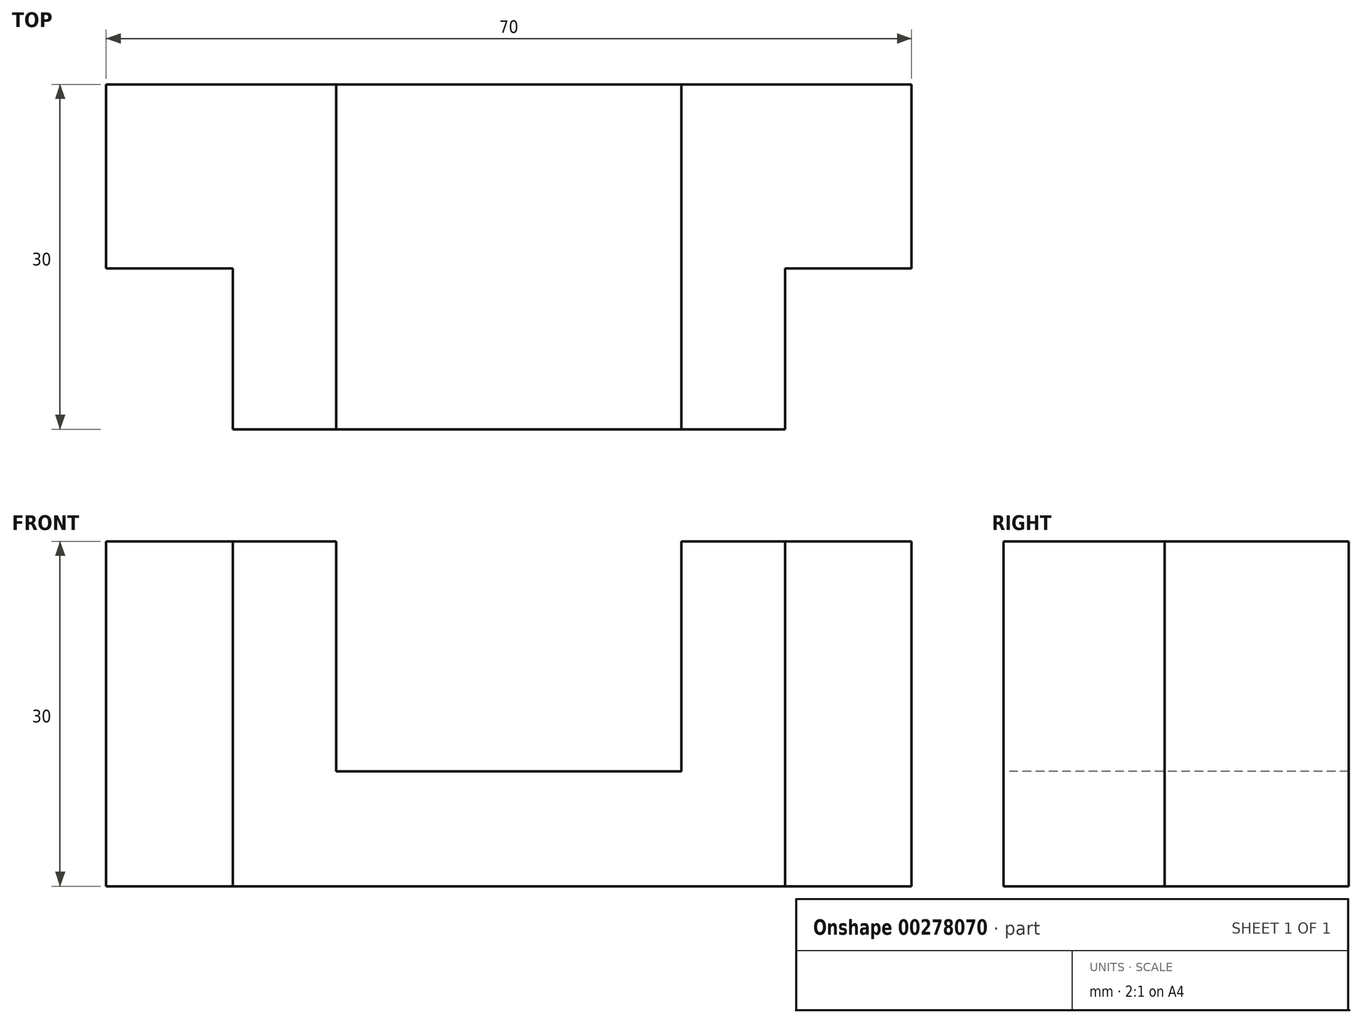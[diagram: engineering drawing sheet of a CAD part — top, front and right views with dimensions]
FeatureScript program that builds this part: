
annotation { "Feature Type Name" : "Feature", "Feature Type Description" : "" }
export const myFeature = defineFeature(function(context is Context, id is Id, definition is map)
    precondition{}
    {
        {
            var Q0;
            Q0=qCreatedBy(makeId("Front.planeOp"),FACE);
            var sketch = newSketch(context, id + "F0", { "sketchPlane" : qUnion([Q0])});
            skLineSegment(sketch, "E0", {"start": v(-35, 15) * mm, "end": v(-35, -15) * mm});
            skLineSegment(sketch, "E1", {"start": v(-35, -15) * mm, "end": v(35, -15) * mm});
            skLineSegment(sketch, "E2", {"start": v(35, -15) * mm, "end": v(35, 15) * mm});
            skLineSegment(sketch, "E3", {"start": v(35, 15) * mm, "end": v(-35, 15) * mm});
            skSolve(sketch);
        }
        {
            var Q0;
            Q0 = qSketchRegion(id + "F0", true);
            extrude(context, id + "F1", {"entities" : qUnion([Q0]), "depth" : 30 * mm});
        }
        {
            var Q0;
            Q0=makeQuery(id+"F1.opExtrude","SWEPT_FACE",FACE,{"disambiguationData":[OSD([sQuery(id+"F0.wireOp",EDGE,"E3")])]});
            var sketch = newSketch(context, id + "F2", { "sketchPlane" : qUnion([Q0])});
            skLineSegment(sketch, "E4", {"start": v(-15, 0) * mm, "end": v(-15, -30) * mm});
            skLineSegment(sketch, "E5", {"start": v(-15, -30) * mm, "end": v(15, -30) * mm});
            skLineSegment(sketch, "E6", {"start": v(15, -30) * mm, "end": v(15, 0) * mm});
            skLineSegment(sketch, "E7", {"start": v(-15, 0) * mm, "end": v(15, 0) * mm});
            skSolve(sketch);
        }
        {
            var Q0;
            Q0=makeQuery(id+"F2.imprint","IMPRINT",FACE,{"disambiguationData":[TD([[makeQuery(id+"F2.imprint","IMPRINT",EDGE,{"derivedFrom":sQuery(id+"F2.wireOp",EDGE,"E4")}),1.0]])]});
            extrude(context, id + "F3", {"entities" : qUnion([Q0]), "operationType" : NewBodyOperationType.REMOVE, "oppositeDirection" : true, "depth" : 20 * mm});
        }
        {
            var Q0;
            Q0=makeQuery(id+"F2.imprint","IMPRINT",FACE,{"disambiguationData":[TD([[makeQuery(id+"F2.imprint","IMPRINT",EDGE,{"derivedFrom":sQuery(id+"F2.wireOp",EDGE,"E4")}),1.0]])]});
            extrude(context, id + "F4", {"entities" : qUnion([Q0]), "operationType" : NewBodyOperationType.REMOVE, "oppositeDirection" : true, "depth" : 20 * mm});
        }
        {
            var Q0;
            {var subQ0=sQuery(id+"F0.wireOp",EDGE,"E3");var subQ1=sQuery(id+"F0.wireOp",EDGE,"E2");Q0=makeQuery(id+"F4.boolean.opBoolean","SPLIT",FACE,{"disambiguationData":[TD([makeQuery(id+"F1.opExtrude","SWEPT_FACE",FACE,{"disambiguationData":[OSD([subQ1])]})])],"derivedFrom":makeQuery(id+"F1.opExtrude","SWEPT_FACE",FACE,{"disambiguationData":[OSD([subQ0])]})});}
            var sketch = newSketch(context, id + "F5", { "sketchPlane" : qUnion([Q0])});
            skLineSegment(sketch, "E8", {"start": v(24, -30) * mm, "end": v(24, -16) * mm});
            skLineSegment(sketch, "E9", {"start": v(24, -16) * mm, "end": v(35, -16) * mm});
            skLineSegment(sketch, "E10", {"start": v(24, -30) * mm, "end": v(35, -30) * mm});
            skLineSegment(sketch, "E11", {"start": v(35, -30) * mm, "end": v(35, -16) * mm});
            skSolve(sketch);
        }
        {
            var Q0;
            Q0=makeQuery(id+"F5.imprint","IMPRINT",FACE,{"disambiguationData":[TD([[makeQuery(id+"F5.imprint","IMPRINT",EDGE,{"derivedFrom":sQuery(id+"F5.wireOp",EDGE,"E8")}),-1.0]])]});
            extrude(context, id + "F6", {"entities" : qUnion([Q0]), "operationType" : NewBodyOperationType.REMOVE, "oppositeDirection" : true, "depth" : 30 * mm});
        }
        {
            var Q0;
            {var subQ0=sQuery(id+"F0.wireOp",EDGE,"E0");var subQ1=sQuery(id+"F0.wireOp",EDGE,"E3");Q0=makeQuery(id+"F4.boolean.opBoolean","SPLIT",FACE,{"disambiguationData":[TD([makeQuery(id+"F1.opExtrude","SWEPT_FACE",FACE,{"disambiguationData":[OSD([subQ0])]})])],"derivedFrom":makeQuery(id+"F1.opExtrude","SWEPT_FACE",FACE,{"disambiguationData":[OSD([subQ1])]})});}
            var sketch = newSketch(context, id + "F7", { "sketchPlane" : qUnion([Q0])});
            skLineSegment(sketch, "E12", {"start": v(-24, -30) * mm, "end": v(-24, -16) * mm});
            skLineSegment(sketch, "E13", {"start": v(-24, -16) * mm, "end": v(-35, -16) * mm});
            skLineSegment(sketch, "E14", {"start": v(-35, -16) * mm, "end": v(-35, -30) * mm});
            skLineSegment(sketch, "E15", {"start": v(-35, -30) * mm, "end": v(-24, -30) * mm});
            skSolve(sketch);
        }
        {
            var Q0;
            Q0=makeQuery(id+"F7.imprint","IMPRINT",FACE,{"disambiguationData":[TD([[makeQuery(id+"F7.imprint","IMPRINT",EDGE,{"derivedFrom":sQuery(id+"F7.wireOp",EDGE,"E12")}),1.0]])]});
            extrude(context, id + "F8", {"entities" : qUnion([Q0]), "operationType" : NewBodyOperationType.REMOVE, "oppositeDirection" : true, "depth" : 30 * mm});
        }
    });
